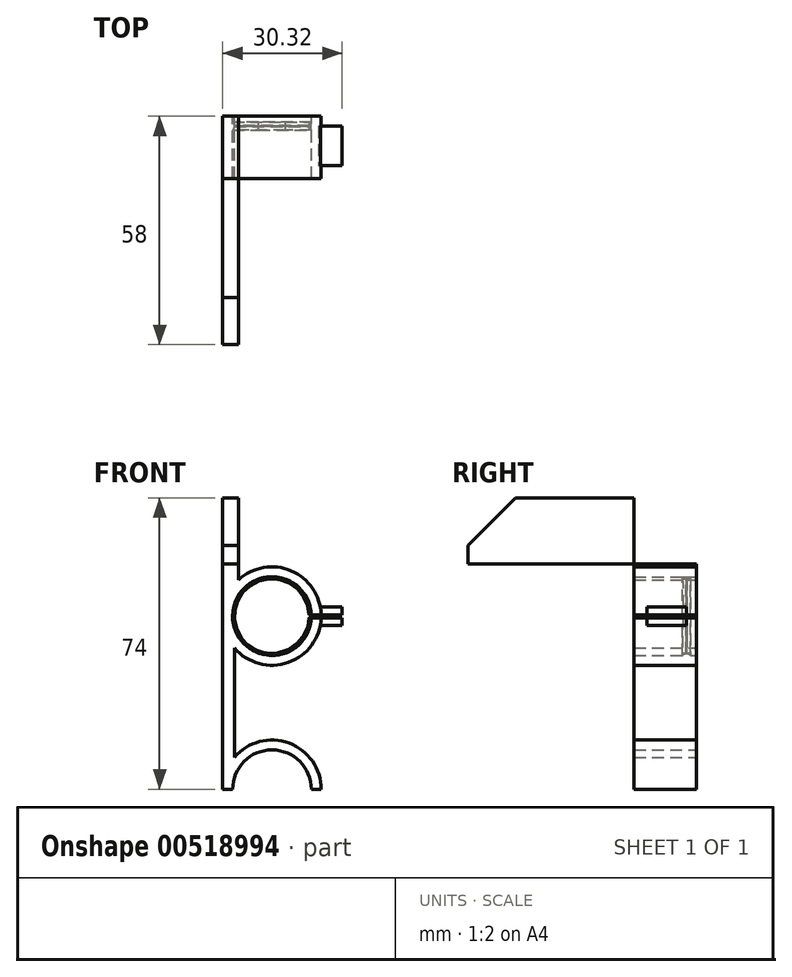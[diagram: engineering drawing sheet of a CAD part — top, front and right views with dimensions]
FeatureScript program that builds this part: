
annotation { "Feature Type Name" : "Feature", "Feature Type Description" : "" }
export const myFeature = defineFeature(function(context is Context, id is Id, definition is map)
    precondition{}
    {
        {
            var Q0;
            Q0=qCreatedBy(makeId("Front.planeOp"),FACE);
            var sketch = newSketch(context, id + "F0", { "sketchPlane" : qUnion([Q0])});
            skCircle(sketch, "E0", {"center": v(0, 25.71) * mm, "radius": 5 * mm, "construction": true});
            skCircle(sketch, "E1", {"center": v(0, -18.29) * mm, "radius": 5 * mm, "construction": true});
            skCircle(sketch, "E2", {"center": v(0, 25.71) * mm, "radius": 9.5 * mm, "construction": true});
            skCircle(sketch, "E3", {"center": v(0, -18.29) * mm, "radius": 9.5 * mm, "construction": true});
            skCircle(sketch, "E4", {"center": v(0, 25.71) * mm, "radius": 10 * mm});
            skCircle(sketch, "E5", {"center": v(0, 25.71) * mm, "radius": 12.5 * mm});
            skArc(sketch, "E6", {"start": v(10, -18.29) * mm, "mid": v(0, -8.29) * mm, "end": v(-10, -18.29) * mm});
            skArc(sketch, "E7", {"start": v(12.5, -18.29) * mm, "mid": v(0, -5.79) * mm, "end": v(-12.5, -18.29) * mm});
            skLineSegment(sketch, "E8", {"start": v(-10, -18.29) * mm, "end": v(-12.5, -18.29) * mm});
            skLineSegment(sketch, "E9", {"start": v(10, -18.29) * mm, "end": v(12.5, -18.29) * mm});
            skLineSegment(sketch, "E10", {"start": v(-12.5, -18.29) * mm, "end": v(-12.5, 25.71) * mm});
            skLineSegment(sketch, "E11", {"start": v(-9.5, -10.16) * mm, "end": v(-9.5, 17.59) * mm});
            skLineSegment(sketch, "E12", {"start": v(-12.5, 25.71) * mm, "end": v(-12.5, 55.71) * mm});
            skLineSegment(sketch, "E13", {"start": v(-12.5, 55.71) * mm, "end": v(-8.5, 55.71) * mm});
            skLineSegment(sketch, "E14", {"start": v(-8.5, 55.71) * mm, "end": v(-8.5, 34.88) * mm});
            skLineSegment(sketch, "E15", {"start": v(10, 26.05) * mm, "end": v(12.5, 26.05) * mm});
            skLineSegment(sketch, "E16", {"start": v(10, 25.3) * mm, "end": v(12.5, 25.3) * mm});
            skSolve(sketch);
        }
        {
            var Q0;
            {var subQ0=sQuery(id+"F0.wireOp",EDGE,"E12");Q0=makeQuery(id+"F0.imprint","IMPRINT",FACE,{"disambiguationData":[TD([[makeQuery(id+"F0.imprint","IMPRINT",EDGE,{"derivedFrom":subQ0}),-1.0]])]});}
            var Q1;
            {var subQ0=sQuery(id+"F0.wireOp",EDGE,"E10");Q1=makeQuery(id+"F0.imprint","IMPRINT",FACE,{"disambiguationData":[TD([[makeQuery(id+"F0.imprint","IMPRINT",EDGE,{"derivedFrom":subQ0}),-1.0]])]});}
            var Q2;
            Q2=makeQuery(id+"F0.imprint","IMPRINT",FACE,{"disambiguationData":[TD([[makeQuery(id+"F0.imprint","IMPRINT",EDGE,{"derivedFrom":sQuery(id+"F0.wireOp",EDGE,"E6")}),-1.0]])]});
            var Q3;
            {var subQ4=sQuery(id+"F0.wireOp",EDGE,"E15");Q3=makeQuery(id+"F0.imprint","IMPRINT",FACE,{"disambiguationData":[TD([[makeQuery(id+"F0.imprint","IMPRINT",EDGE,{"derivedFrom":subQ4}),1.0]])]});}
            extrude(context, id + "F1", {"entities" : qUnion([Q0, Q1, Q2, Q3]), "depth" : 58 * mm, "offsetDistance" : 25 * mm});
        }
        {
            var Q0;
            Q0=makeQuery(id+"F1.opExtrude","CAP_FACE",FACE,{"disambiguationData":[OSD([sQuery(id+"F0.wireOp",EDGE,"E4"),sQuery(id+"F0.wireOp",EDGE,"E5"),sQuery(id+"F0.wireOp",EDGE,"E6"),sQuery(id+"F0.wireOp",EDGE,"E7"),sQuery(id+"F0.wireOp",EDGE,"E8"),sQuery(id+"F0.wireOp",EDGE,"E9"),sQuery(id+"F0.wireOp",EDGE,"E10"),sQuery(id+"F0.wireOp",EDGE,"E11"),sQuery(id+"F0.wireOp",EDGE,"E12"),sQuery(id+"F0.wireOp",EDGE,"E13"),sQuery(id+"F0.wireOp",EDGE,"E14")])],"isStart":false});
            var sketch = newSketch(context, id + "F2", { "sketchPlane" : qUnion([Q0])});
            skSolve(sketch);
        }
        {
            var Q0;
            Q0=makeQuery(id+"F2.imprint","IMPRINT",FACE,{"disambiguationData":[TD([[makeQuery(id+"F2.imprint","IMPRINT",EDGE,{"derivedFrom":makeQuery(id+"F1.opExtrude","CAP_EDGE",EDGE,{"disambiguationData":[OSD([sQuery(id+"F0.wireOp",EDGE,"E4")])],"isStart":false})}),-1.0]])]});
            cPlane(context, id + "F3", {"entities" : qUnion([Q0]), "cplaneType" : CPlaneType.OFFSET, "offset" : 3.5 * mm, "oppositeDirection" : true, "width" : 150 * mm, "height" : 150 * mm});
        }
        {
            var Q0;
            Q0=qCreatedBy(id+"F3.planeOp",FACE);
            var sketch = newSketch(context, id + "F4", { "sketchPlane" : qUnion([Q0])});
            skArc(sketch, "E17", {"start": v(10, 26.05) * mm, "mid": v(-10, 25.75) * mm, "end": v(10, 25.3) * mm});
            skArc(sketch, "E18", {"start": v(9.5, 26.05) * mm, "mid": v(-9.5, 25.75) * mm, "end": v(9.5, 25.3) * mm});
            skLineSegment(sketch, "E19", {"start": v(10, 26.05) * mm, "end": v(9.5, 26.05) * mm});
            skLineSegment(sketch, "E20", {"start": v(9.5, 25.3) * mm, "end": v(10, 25.3) * mm});
            skLineSegment(sketch, "E21.bottom", {"start": v(11.88, 26.05) * mm, "end": v(17.88, 26.05) * mm});
            skLineSegment(sketch, "E21.top", {"start": v(11.88, 28.05) * mm, "end": v(17.88, 28.05) * mm});
            skLineSegment(sketch, "E21.left", {"start": v(11.88, 26.05) * mm, "end": v(11.88, 28.05) * mm});
            skLineSegment(sketch, "E21.right", {"start": v(17.88, 26.05) * mm, "end": v(17.88, 28.05) * mm});
            skLineSegment(sketch, "E22.bottom", {"start": v(11.91, 25.3) * mm, "end": v(17.88, 25.3) * mm});
            skLineSegment(sketch, "E22.top", {"start": v(11.91, 23.3) * mm, "end": v(17.88, 23.3) * mm});
            skLineSegment(sketch, "E22.left", {"start": v(11.91, 25.3) * mm, "end": v(11.91, 23.3) * mm});
            skLineSegment(sketch, "E22.right", {"start": v(17.88, 25.3) * mm, "end": v(17.88, 23.3) * mm});
            skArc(sketch, "E23", {"start": v(-10, -18.29) * mm, "mid": v(0, -8.29) * mm, "end": v(10, -18.29) * mm});
            skArc(sketch, "E24", {"start": v(-9.5, -18.29) * mm, "mid": v(0, -8.79) * mm, "end": v(9.5, -18.29) * mm});
            skLineSegment(sketch, "E25", {"start": v(10, -18.29) * mm, "end": v(9.5, -18.29) * mm});
            skLineSegment(sketch, "E26", {"start": v(-9.5, -18.29) * mm, "end": v(-10, -18.29) * mm});
            skSolve(sketch);
        }
        {
            var Q0;
            Q0=makeQuery(id+"F4.imprint","IMPRINT",FACE,{"disambiguationData":[TD([[makeQuery(id+"F4.imprint","IMPRINT",EDGE,{"derivedFrom":sQuery(id+"F4.wireOp",EDGE,"E17")}),1.0]])]});
            var Q1;
            Q1=makeQuery(id+"F4.imprint","IMPRINT",FACE,{"disambiguationData":[TD([[makeQuery(id+"F4.imprint","IMPRINT",EDGE,{"derivedFrom":sQuery(id+"F4.wireOp",EDGE,"E23")}),-1.0]])]});
            extrude(context, id + "F5", {"entities" : qUnion([Q0, Q1]), "operationType" : NewBodyOperationType.ADD, "depth" : 2 * mm, "offsetDistance" : 25 * mm, "symmetric" : true});
        }
        {
            var Q0;
            Q0=makeQuery(id+"F4.imprint","IMPRINT",FACE,{"disambiguationData":[TD([[makeQuery(id+"F4.imprint","IMPRINT",EDGE,{"derivedFrom":sQuery(id+"F4.wireOp",EDGE,"E21.bottom")}),1.0]])]});
            var Q1;
            Q1=makeQuery(id+"F4.imprint","IMPRINT",FACE,{"disambiguationData":[TD([[makeQuery(id+"F4.imprint","IMPRINT",EDGE,{"derivedFrom":sQuery(id+"F4.wireOp",EDGE,"E22.bottom")}),-1.0]])]});
            extrude(context, id + "F6", {"entities" : qUnion([Q0, Q1]), "operationType" : NewBodyOperationType.ADD, "oppositeDirection" : true, "depth" : 10 * mm, "offsetDistance" : 25 * mm});
        }
        {
            var Q0;
            Q0=makeQuery(id+"F6.opExtrude","CAP_EDGE",EDGE,{"disambiguationData":[OSD([sQuery(id+"F4.wireOp",EDGE,"E21.right")])],"isStart":true});
            var Q1;
            Q1=makeQuery(id+"F6.opExtrude","CAP_EDGE",EDGE,{"disambiguationData":[OSD([sQuery(id+"F4.wireOp",EDGE,"E22.right")])],"isStart":true});
            chamfer(context, id + "F7", {"entities" : qUnion([Q0, Q1]), "width" : 5 * mm, "tangentPropagation" : true});
        }
        {
            var Q0;
            Q0=makeQuery(id+"F6.opExtrude","SWEPT_FACE",FACE,{"disambiguationData":[OSD([sQuery(id+"F4.wireOp",EDGE,"E21.top")])]});
            var sketch = newSketch(context, id + "F8", { "sketchPlane" : qUnion([Q0])});
            skCircle(sketch, "E27", {"center": v(15.04, -69.24) * mm, "radius": 1.5 * mm});
            skSolve(sketch);
        }
        {
            var Q0;
            Q0=makeQuery(id+"F8.imprint","IMPRINT",FACE,{"disambiguationData":[TD([[makeQuery(id+"F8.imprint","IMPRINT",EDGE,{"derivedFrom":sQuery(id+"F8.wireOp",EDGE,"E27")}),1.0]])]});
            extrude(context, id + "F9", {"entities" : qUnion([Q0]), "operationType" : NewBodyOperationType.REMOVE, "oppositeDirection" : true, "depth" : 25 * mm, "offsetDistance" : 25 * mm});
        }
        {
            var Q0;
            Q0=qCreatedBy(id+"F3.planeOp",FACE);
            cPlane(context, id + "F10", {"entities" : qUnion([Q0]), "cplaneType" : CPlaneType.OFFSET, "offset" : 52 * mm, "oppositeDirection" : true, "width" : 150 * mm, "height" : 150 * mm});
        }
        {
            var Q0;
            Q0=qCreatedBy(id+"F10.planeOp",FACE);
            var sketch = newSketch(context, id + "F11", { "sketchPlane" : qUnion([Q0])});
            skArc(sketch, "E28", {"start": v(9.94, 26.03) * mm, "mid": v(-10.05, 25.73) * mm, "end": v(9.94, 25.28) * mm});
            skArc(sketch, "E29", {"start": v(9.44, 26.03) * mm, "mid": v(-9.55, 25.73) * mm, "end": v(9.44, 25.28) * mm});
            skLineSegment(sketch, "E30", {"start": v(9.94, 26.03) * mm, "end": v(9.44, 26.03) * mm});
            skLineSegment(sketch, "E31", {"start": v(9.44, 25.28) * mm, "end": v(9.94, 25.28) * mm});
            skLineSegment(sketch, "E32.bottom", {"start": v(11.82, 26.03) * mm, "end": v(17.82, 26.03) * mm});
            skLineSegment(sketch, "E32.top", {"start": v(11.82, 28.03) * mm, "end": v(17.82, 28.03) * mm});
            skLineSegment(sketch, "E32.left", {"start": v(11.82, 26.03) * mm, "end": v(11.82, 28.03) * mm});
            skLineSegment(sketch, "E32.right", {"start": v(17.82, 26.03) * mm, "end": v(17.82, 28.03) * mm});
            skLineSegment(sketch, "E33.bottom", {"start": v(11.86, 25.28) * mm, "end": v(17.82, 25.28) * mm});
            skLineSegment(sketch, "E33.top", {"start": v(11.86, 23.28) * mm, "end": v(17.82, 23.28) * mm});
            skLineSegment(sketch, "E33.left", {"start": v(11.86, 25.28) * mm, "end": v(11.86, 23.28) * mm});
            skLineSegment(sketch, "E33.right", {"start": v(17.82, 25.28) * mm, "end": v(17.82, 23.28) * mm});
            skArc(sketch, "E34", {"start": v(-10, -18.29) * mm, "mid": v(0, -8.29) * mm, "end": v(10, -18.29) * mm});
            skArc(sketch, "E35", {"start": v(-9.5, -18.29) * mm, "mid": v(0, -8.79) * mm, "end": v(9.5, -18.29) * mm});
            skLineSegment(sketch, "E36", {"start": v(10, -18.29) * mm, "end": v(9.5, -18.29) * mm});
            skLineSegment(sketch, "E37", {"start": v(-9.5, -18.29) * mm, "end": v(-10, -18.29) * mm});
            skSolve(sketch);
        }
        {
            var Q0;
            Q0=makeQuery(id+"F11.imprint","IMPRINT",FACE,{"disambiguationData":[TD([[makeQuery(id+"F11.imprint","IMPRINT",EDGE,{"derivedFrom":sQuery(id+"F11.wireOp",EDGE,"E34")}),-1.0]])]});
            var Q1;
            Q1=makeQuery(id+"F11.imprint","IMPRINT",FACE,{"disambiguationData":[TD([[makeQuery(id+"F11.imprint","IMPRINT",EDGE,{"derivedFrom":sQuery(id+"F11.wireOp",EDGE,"E28")}),1.0]])]});
            extrude(context, id + "F12", {"entities" : qUnion([Q0, Q1]), "operationType" : NewBodyOperationType.ADD, "depth" : 2 * mm, "offsetDistance" : 25 * mm, "symmetric" : true});
        }
        {
            var Q0;
            Q0=makeQuery(id+"F5.opExtrude","CAP_EDGE",EDGE,{"disambiguationData":[OSD([sQuery(id+"F4.wireOp",EDGE,"E18")])],"isStart":false});
            var Q1;
            Q1=makeQuery(id+"F5.opExtrude","CAP_EDGE",EDGE,{"disambiguationData":[OSD([sQuery(id+"F4.wireOp",EDGE,"E18")])],"isStart":true});
            var Q2;
            Q2=makeQuery(id+"F5.opExtrude","CAP_EDGE",EDGE,{"disambiguationData":[OSD([sQuery(id+"F4.wireOp",EDGE,"E24")])],"isStart":false});
            var Q3;
            Q3=makeQuery(id+"F5.opExtrude","CAP_EDGE",EDGE,{"disambiguationData":[OSD([sQuery(id+"F4.wireOp",EDGE,"E24")])],"isStart":true});
            var Q4;
            Q4=makeQuery(id+"F12.opExtrude","CAP_EDGE",EDGE,{"disambiguationData":[OSD([sQuery(id+"F11.wireOp",EDGE,"E29")])],"isStart":true});
            var Q5;
            Q5=makeQuery(id+"F12.opExtrude","CAP_EDGE",EDGE,{"disambiguationData":[OSD([sQuery(id+"F11.wireOp",EDGE,"E29")])],"isStart":false});
            var Q6;
            Q6=makeQuery(id+"F12.opExtrude","CAP_EDGE",EDGE,{"disambiguationData":[OSD([sQuery(id+"F11.wireOp",EDGE,"E35")])],"isStart":true});
            var Q7;
            Q7=makeQuery(id+"F12.opExtrude","CAP_EDGE",EDGE,{"disambiguationData":[OSD([sQuery(id+"F11.wireOp",EDGE,"E35")])],"isStart":false});
            fillet(context, id + "F13", {"entities" : qUnion([Q0, Q1, Q2, Q3, Q4, Q5, Q6, Q7]), "radius" : 1 * mm, "rho" : 0.5, "crossSection" : FilletCrossSection.CONIC, "allowEdgeOverflow" : false});
        }
        {
            var Q0;
            Q0=makeQuery(id+"F11.imprint","IMPRINT",FACE,{"disambiguationData":[TD([[makeQuery(id+"F11.imprint","IMPRINT",EDGE,{"derivedFrom":sQuery(id+"F11.wireOp",EDGE,"E32.bottom")}),1.0]])]});
            var Q1;
            Q1=makeQuery(id+"F11.imprint","IMPRINT",FACE,{"disambiguationData":[TD([[makeQuery(id+"F11.imprint","IMPRINT",EDGE,{"derivedFrom":sQuery(id+"F11.wireOp",EDGE,"E33.bottom")}),-1.0]])]});
            extrude(context, id + "F14", {"entities" : qUnion([Q0, Q1]), "operationType" : NewBodyOperationType.ADD, "depth" : 10 * mm, "offsetDistance" : 25 * mm});
        }
        {
            var Q0;
            Q0=makeQuery(id+"F1.opExtrude","CAP_EDGE",EDGE,{"disambiguationData":[OSD([sQuery(id+"F0.wireOp",EDGE,"E13")])],"isStart":false});
            var Q1;
            Q1=makeQuery(id+"F1.opExtrude","CAP_EDGE",EDGE,{"disambiguationData":[OSD([sQuery(id+"F0.wireOp",EDGE,"E13")])],"isStart":true});
            chamfer(context, id + "F15", {"entities" : qUnion([Q0, Q1]), "width" : 12 * mm, "tangentPropagation" : true});
        }
        {
            var Q0;
            Q0=qCreatedBy(makeId("Right.planeOp"),FACE);
            var sketch = newSketch(context, id + "F16", { "sketchPlane" : qUnion([Q0])});
            skLineSegment(sketch, "E38.bottom", {"start": v(-66.17, 66.07) * mm, "end": v(-15.85, 66.07) * mm});
            skLineSegment(sketch, "E38.top", {"start": v(-66.17, -27.83) * mm, "end": v(-15.85, -27.83) * mm});
            skLineSegment(sketch, "E38.left", {"start": v(-66.17, 66.07) * mm, "end": v(-66.17, -27.83) * mm});
            skLineSegment(sketch, "E38.right", {"start": v(-15.85, 66.07) * mm, "end": v(-15.85, -27.83) * mm});
            skLineSegment(sketch, "E39.bottom", {"start": v(14.07, 38.93) * mm, "end": v(-66.17, 38.93) * mm});
            skLineSegment(sketch, "E39.top", {"start": v(14.07, 66.07) * mm, "end": v(-66.17, 66.07) * mm});
            skLineSegment(sketch, "E39.left", {"start": v(14.07, 38.93) * mm, "end": v(14.07, 66.07) * mm});
            skLineSegment(sketch, "E39.right", {"start": v(-66.17, 38.93) * mm, "end": v(-66.17, 66.07) * mm});
            skSolve(sketch);
        }
        {
            var Q0;
            {var subQ5=sQuery(id+"F16.wireOp",EDGE,"E39.right");Q0=makeQuery(id+"F16.imprint","IMPRINT",FACE,{"disambiguationData":[TD([[makeQuery(id+"F16.imprint","IMPRINT",EDGE,{"derivedFrom":subQ5}),-1.0]])]});}
            var Q1;
            {var subQ5=sQuery(id+"F16.wireOp",EDGE,"E39.left");Q1=makeQuery(id+"F16.imprint","IMPRINT",FACE,{"disambiguationData":[TD([[makeQuery(id+"F16.imprint","IMPRINT",EDGE,{"derivedFrom":subQ5}),1.0]])]});}
            var Q2;
            {var subQ0=sQuery(id+"F16.wireOp",EDGE,"E38.top");Q2=makeQuery(id+"F16.imprint","IMPRINT",FACE,{"disambiguationData":[TD([[makeQuery(id+"F16.imprint","IMPRINT",EDGE,{"derivedFrom":subQ0}),1.0]])]});}
            extrude(context, id + "F17", {"entities" : qUnion([Q0, Q1, Q2]), "operationType" : NewBodyOperationType.REMOVE, "depth" : 40 * mm, "offsetDistance" : 25 * mm, "symmetric" : true});
        }
    });
